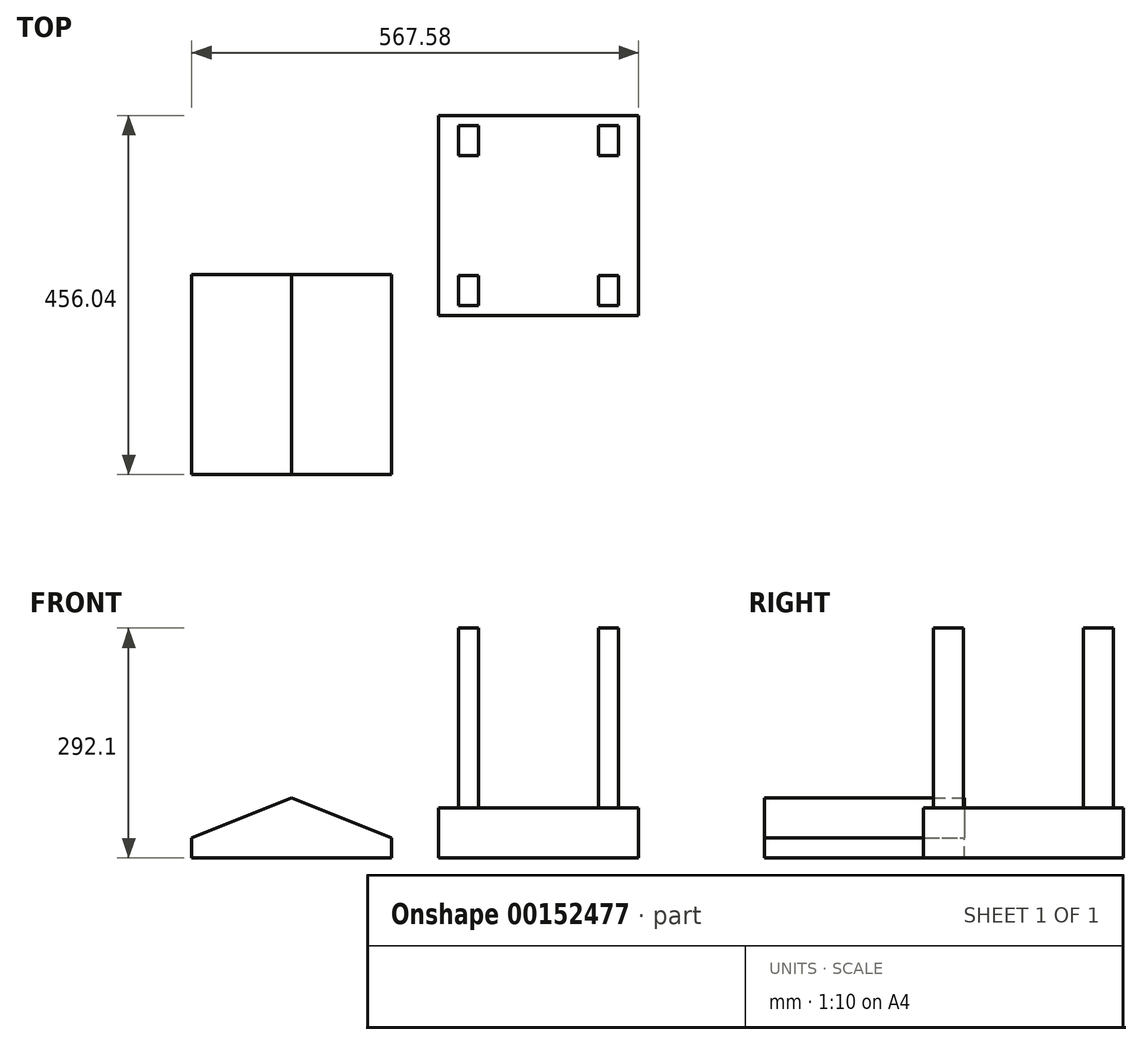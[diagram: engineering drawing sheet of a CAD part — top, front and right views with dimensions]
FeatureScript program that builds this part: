
annotation { "Feature Type Name" : "Feature", "Feature Type Description" : "" }
export const myFeature = defineFeature(function(context is Context, id is Id, definition is map)
    precondition{}
    {
        {
            var Q0;
            Q0=qCreatedBy(makeId("Top.planeOp"),FACE);
            var sketch = newSketch(context, id + "F0", { "sketchPlane" : qUnion([Q0])});
            skLineSegment(sketch, "E0.bottom", {"start": v(-63.63, -51.96) * mm, "end": v(190.37, -51.96) * mm});
            skLineSegment(sketch, "E0.top", {"start": v(-63.63, 202.04) * mm, "end": v(190.37, 202.04) * mm});
            skLineSegment(sketch, "E0.left", {"start": v(-63.63, -51.96) * mm, "end": v(-63.63, 202.04) * mm});
            skLineSegment(sketch, "E0.right", {"start": v(190.37, -51.96) * mm, "end": v(190.37, 202.04) * mm});
            skSolve(sketch);
        }
        {
            var Q0;
            Q0 = qSketchRegion(id + "F0", true);
            extrude(context, id + "F1", {"entities" : qUnion([Q0]), "depth" : 63.5 * mm});
        }
        {
            var Q0;
            Q0=makeQuery(id+"F1.opExtrude","CAP_FACE",FACE,{"disambiguationData":[OSD([sQuery(id+"F0.wireOp",EDGE,"E0.bottom"),sQuery(id+"F0.wireOp",EDGE,"E0.top"),sQuery(id+"F0.wireOp",EDGE,"E0.left"),sQuery(id+"F0.wireOp",EDGE,"E0.right")])],"isStart":false});
            var sketch = newSketch(context, id + "F2", { "sketchPlane" : qUnion([Q0])});
            skLineSegment(sketch, "E1.bottom", {"start": v(-38.23, 189.34) * mm, "end": v(-12.83, 189.34) * mm});
            skLineSegment(sketch, "E1.top", {"start": v(-38.23, 151.24) * mm, "end": v(-12.83, 151.24) * mm});
            skLineSegment(sketch, "E1.left", {"start": v(-38.23, 189.34) * mm, "end": v(-38.23, 151.24) * mm});
            skLineSegment(sketch, "E1.right", {"start": v(-12.83, 189.34) * mm, "end": v(-12.83, 151.24) * mm});
            skLineSegment(sketch, "E2.bottom", {"start": v(-38.23, -39.26) * mm, "end": v(-12.83, -39.26) * mm});
            skLineSegment(sketch, "E2.top", {"start": v(-38.23, -1.16) * mm, "end": v(-12.83, -1.16) * mm});
            skLineSegment(sketch, "E2.left", {"start": v(-38.23, -39.26) * mm, "end": v(-38.23, -1.16) * mm});
            skLineSegment(sketch, "E2.right", {"start": v(-12.83, -39.26) * mm, "end": v(-12.83, -1.16) * mm});
            skLineSegment(sketch, "E3.bottom", {"start": v(164.97, -39.26) * mm, "end": v(139.57, -39.26) * mm});
            skLineSegment(sketch, "E3.top", {"start": v(164.97, -1.16) * mm, "end": v(139.57, -1.16) * mm});
            skLineSegment(sketch, "E3.left", {"start": v(164.97, -39.26) * mm, "end": v(164.97, -1.16) * mm});
            skLineSegment(sketch, "E3.right", {"start": v(139.57, -39.26) * mm, "end": v(139.57, -1.16) * mm});
            skLineSegment(sketch, "E4.bottom", {"start": v(164.97, 189.34) * mm, "end": v(139.57, 189.34) * mm});
            skLineSegment(sketch, "E4.top", {"start": v(164.97, 151.24) * mm, "end": v(139.57, 151.24) * mm});
            skLineSegment(sketch, "E4.left", {"start": v(164.97, 189.34) * mm, "end": v(164.97, 151.24) * mm});
            skLineSegment(sketch, "E4.right", {"start": v(139.57, 189.34) * mm, "end": v(139.57, 151.24) * mm});
            skSolve(sketch);
        }
        {
            var Q0;
            Q0=makeQuery(id+"F2.imprint","IMPRINT",FACE,{"disambiguationData":[TD([[makeQuery(id+"F2.imprint","IMPRINT",EDGE,{"derivedFrom":sQuery(id+"F2.wireOp",EDGE,"E1.bottom")}),-1.0]])]});
            var Q1;
            Q1=makeQuery(id+"F2.imprint","IMPRINT",FACE,{"disambiguationData":[TD([[makeQuery(id+"F2.imprint","IMPRINT",EDGE,{"derivedFrom":sQuery(id+"F2.wireOp",EDGE,"E2.bottom")}),1.0]])]});
            var Q2;
            Q2=makeQuery(id+"F2.imprint","IMPRINT",FACE,{"disambiguationData":[TD([[makeQuery(id+"F2.imprint","IMPRINT",EDGE,{"derivedFrom":sQuery(id+"F2.wireOp",EDGE,"E3.bottom")}),-1.0]])]});
            var Q3;
            Q3=makeQuery(id+"F2.imprint","IMPRINT",FACE,{"disambiguationData":[TD([[makeQuery(id+"F2.imprint","IMPRINT",EDGE,{"derivedFrom":sQuery(id+"F2.wireOp",EDGE,"E4.bottom")}),1.0]])]});
            extrude(context, id + "F3", {"entities" : qUnion([Q0, Q1, Q2, Q3]), "operationType" : NewBodyOperationType.ADD, "depth" : 50.8 * mm});
        }
        {
            var Q0;
            Q0=makeQuery(id+"F3.opExtrude","CAP_FACE",FACE,{"disambiguationData":[OSD([sQuery(id+"F2.wireOp",EDGE,"E2.bottom"),sQuery(id+"F2.wireOp",EDGE,"E2.top"),sQuery(id+"F2.wireOp",EDGE,"E2.left"),sQuery(id+"F2.wireOp",EDGE,"E2.right")])],"isStart":false});
            var Q1;
            Q1=makeQuery(id+"F3.opExtrude","CAP_FACE",FACE,{"disambiguationData":[OSD([sQuery(id+"F2.wireOp",EDGE,"E3.bottom"),sQuery(id+"F2.wireOp",EDGE,"E3.top"),sQuery(id+"F2.wireOp",EDGE,"E3.left"),sQuery(id+"F2.wireOp",EDGE,"E3.right")])],"isStart":false});
            var Q2;
            Q2=makeQuery(id+"F3.opExtrude","CAP_FACE",FACE,{"disambiguationData":[OSD([sQuery(id+"F2.wireOp",EDGE,"E4.bottom"),sQuery(id+"F2.wireOp",EDGE,"E4.top"),sQuery(id+"F2.wireOp",EDGE,"E4.left"),sQuery(id+"F2.wireOp",EDGE,"E4.right")])],"isStart":false});
            var Q3;
            Q3=makeQuery(id+"F3.opExtrude","CAP_FACE",FACE,{"disambiguationData":[OSD([sQuery(id+"F2.wireOp",EDGE,"E1.bottom"),sQuery(id+"F2.wireOp",EDGE,"E1.top"),sQuery(id+"F2.wireOp",EDGE,"E1.left"),sQuery(id+"F2.wireOp",EDGE,"E1.right")])],"isStart":false});
            extrude(context, id + "F4", {"entities" : qUnion([Q0, Q1, Q2, Q3]), "operationType" : NewBodyOperationType.ADD, "depth" : 177.8 * mm});
        }
        {
            var Q0;
            Q0=qCreatedBy(makeId("Front.planeOp"),FACE);
            var sketch = newSketch(context, id + "F5", { "sketchPlane" : qUnion([Q0])});
            skLineSegment(sketch, "E5", {"start": v(-250.2, 0) * mm, "end": v(-250.2, 50.8) * mm});
            skLineSegment(sketch, "E6", {"start": v(-250.2, 0) * mm, "end": v(-123.2, 0) * mm});
            skLineSegment(sketch, "E7", {"start": v(-250.2, 0) * mm, "end": v(-377.2, 0) * mm});
            skLineSegment(sketch, "E8", {"start": v(-250.2, 50.8) * mm, "end": v(-250.2, 76.2) * mm});
            skLineSegment(sketch, "E9", {"start": v(-377.2, 0) * mm, "end": v(-377.2, 25.4) * mm});
            skLineSegment(sketch, "E10", {"start": v(-377.2, 25.4) * mm, "end": v(-123.2, 25.4) * mm});
            skLineSegment(sketch, "E11", {"start": v(-123.2, 25.4) * mm, "end": v(-123.2, 0) * mm});
            skLineSegment(sketch, "E12", {"start": v(-250.2, 76.2) * mm, "end": v(-123.2, 25.4) * mm});
            skLineSegment(sketch, "E13", {"start": v(-250.2, 76.2) * mm, "end": v(-377.2, 25.4) * mm});
            skSolve(sketch);
        }
        {
            var Q0;
            {var subQ0=sQuery(id+"F5.wireOp",EDGE,"E8");Q0=makeQuery(id+"F5.imprint","IMPRINT",FACE,{"disambiguationData":[TD([[makeQuery(id+"F5.imprint","IMPRINT",EDGE,{"derivedFrom":subQ0}),1.0]])]});}
            var Q1;
            {var subQ0=sQuery(id+"F5.wireOp",EDGE,"E8");Q1=makeQuery(id+"F5.imprint","IMPRINT",FACE,{"disambiguationData":[TD([[makeQuery(id+"F5.imprint","IMPRINT",EDGE,{"derivedFrom":subQ0}),-1.0]])]});}
            var Q2;
            {var subQ0=sQuery(id+"F5.wireOp",EDGE,"E6");Q2=makeQuery(id+"F5.imprint","IMPRINT",FACE,{"disambiguationData":[TD([[makeQuery(id+"F5.imprint","IMPRINT",EDGE,{"derivedFrom":subQ0}),1.0]])]});}
            var Q3;
            {var subQ0=sQuery(id+"F5.wireOp",EDGE,"E7");Q3=makeQuery(id+"F5.imprint","IMPRINT",FACE,{"disambiguationData":[TD([[makeQuery(id+"F5.imprint","IMPRINT",EDGE,{"derivedFrom":subQ0}),-1.0]])]});}
            extrude(context, id + "F6", {"entities" : qUnion([Q0, Q1, Q2, Q3]), "depth" : 254 * mm});
        }
    });
